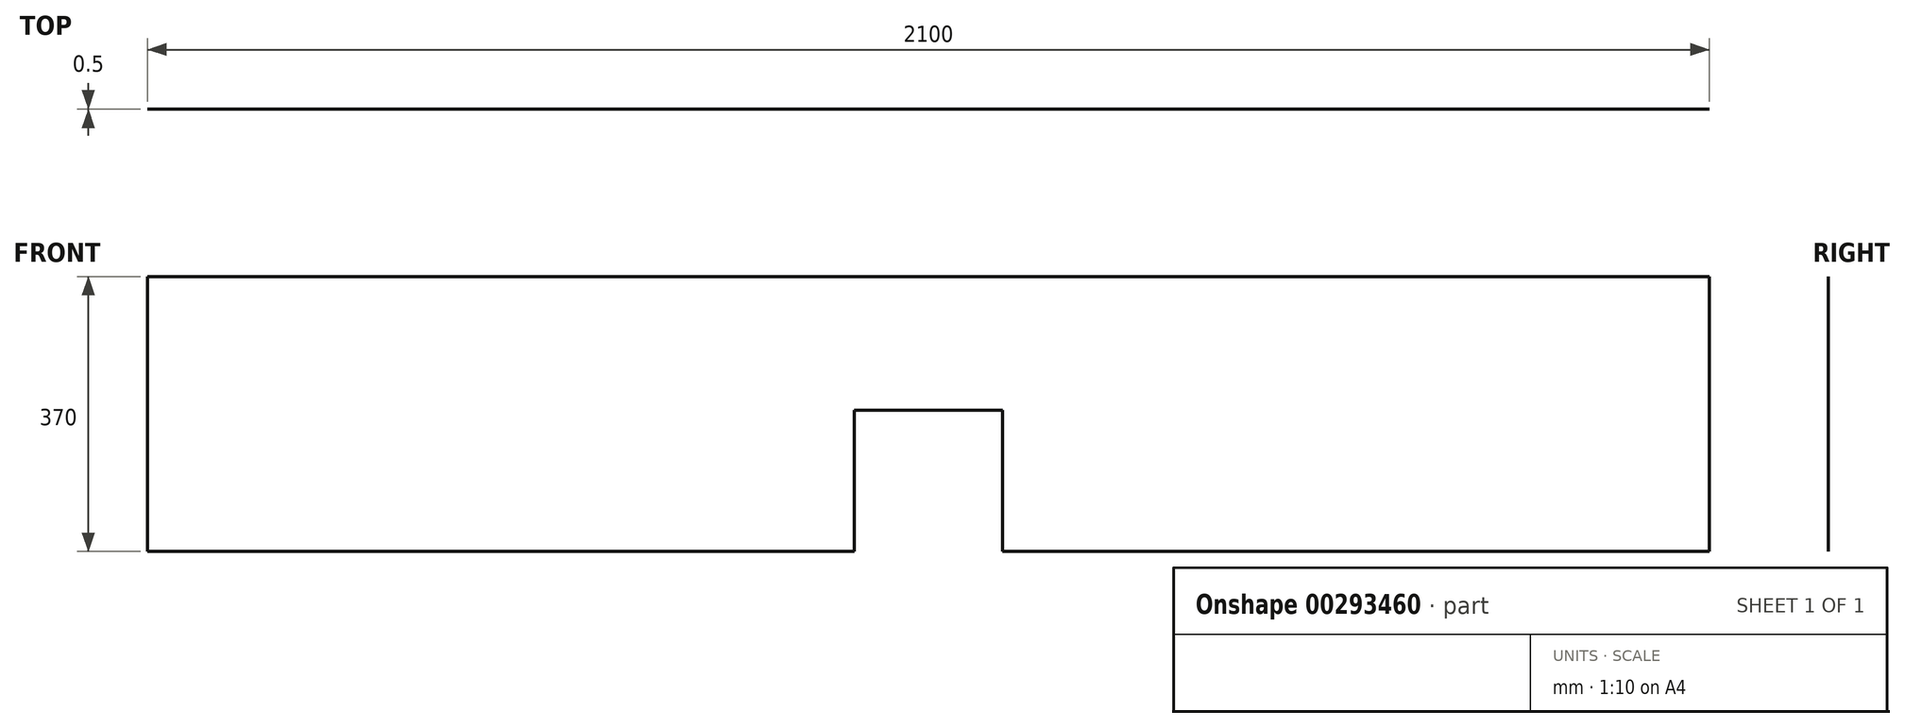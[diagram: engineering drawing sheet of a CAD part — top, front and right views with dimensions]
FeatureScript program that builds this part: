
annotation { "Feature Type Name" : "Feature", "Feature Type Description" : "" }
export const myFeature = defineFeature(function(context is Context, id is Id, definition is map)
    precondition{}
    {
        {
            var Q0;
            Q0=qCreatedBy(makeId("Front.planeOp"),FACE);
            var sketch = newSketch(context, id + "F0", { "sketchPlane" : qUnion([Q0])});
            skLineSegment(sketch, "E0", {"start": v(0, 1109.84) * mm, "end": v(0, -636.9) * mm, "construction": true});
            skLineSegment(sketch, "E1", {"start": v(0, 190) * mm, "end": v(-100, 190) * mm});
            skLineSegment(sketch, "E2", {"start": v(-100, 190) * mm, "end": v(-100, 0) * mm});
            skLineSegment(sketch, "E3", {"start": v(-100, 0) * mm, "end": v(-1050, 0) * mm});
            skLineSegment(sketch, "E4", {"start": v(-1050, 0) * mm, "end": v(-1050, 370) * mm});
            skLineSegment(sketch, "E5", {"start": v(-1050, 370) * mm, "end": v(0, 370) * mm});
            skLineSegment(sketch, "E6.MirrorCS", {"start": v(100, 0) * mm, "end": v(1050, 0) * mm});
            skLineSegment(sketch, "E7.MirrorCS", {"start": v(0, 190) * mm, "end": v(100, 190) * mm});
            skLineSegment(sketch, "E8.MirrorCS", {"start": v(1050, 370) * mm, "end": v(0, 370) * mm});
            skLineSegment(sketch, "E9.MirrorCS", {"start": v(100, 190) * mm, "end": v(100, 0) * mm});
            skLineSegment(sketch, "E10.MirrorCS", {"start": v(1050, 0) * mm, "end": v(1050, 370) * mm});
            skSolve(sketch);
        }
        {
            var Q0;
            Q0=makeQuery(id+"F0.imprint","IMPRINT",FACE,{"disambiguationData":[TD([[makeQuery(id+"F0.imprint","IMPRINT",EDGE,{"derivedFrom":sQuery(id+"F0.wireOp",EDGE,"E1")}),-1.0]])]});
            extrude(context, id + "F1", {"entities" : qUnion([Q0]), "depth" : .5 * mm, "offsetDistance" : 25 * mm});
        }
    });
